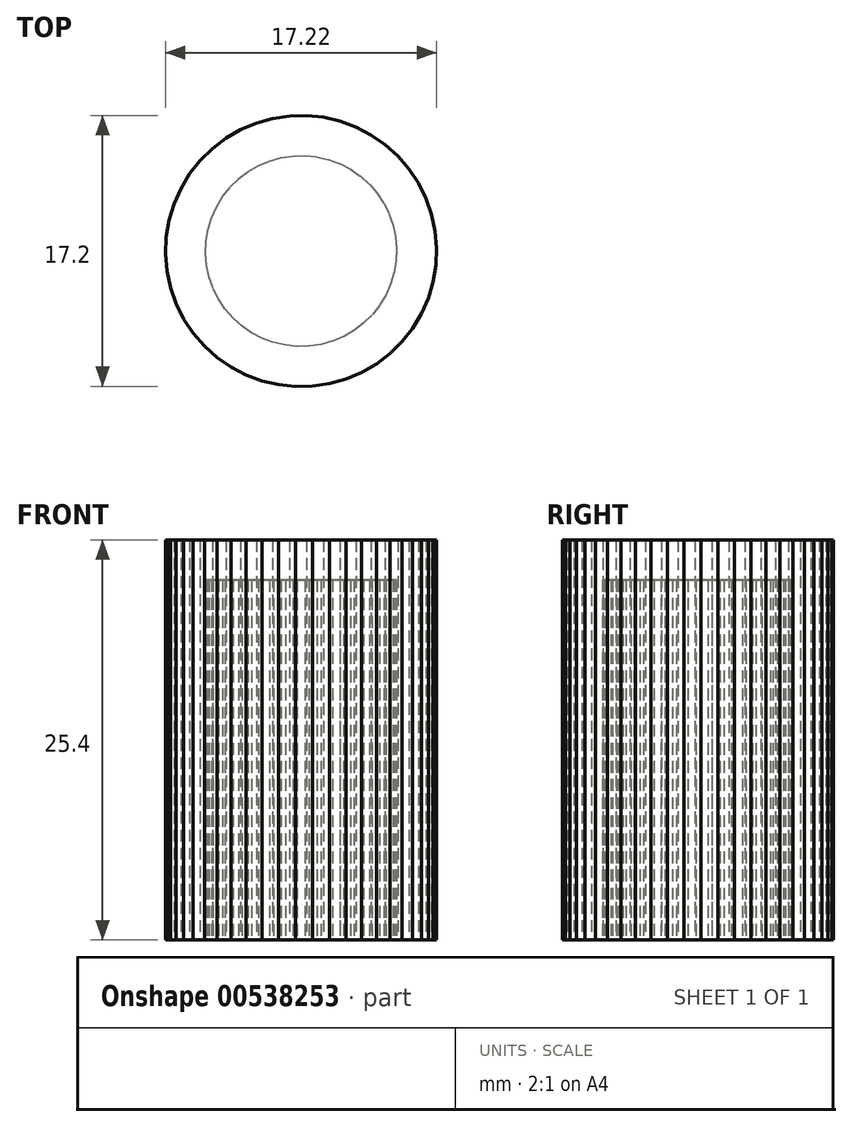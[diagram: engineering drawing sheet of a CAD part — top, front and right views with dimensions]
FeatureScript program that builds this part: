
annotation { "Feature Type Name" : "Feature", "Feature Type Description" : "" }
export const myFeature = defineFeature(function(context is Context, id is Id, definition is map)
    precondition{}
    {
        {
            var Q0;
            Q0=qCreatedBy(makeId("Top.planeOp"),FACE);
            var sketch = newSketch(context, id + "F0", { "sketchPlane" : qUnion([Q0])});
            skCircle(sketch, "E0.cCircle", {"center": v(0, 0) * mm, "radius": 8.61 * mm, "construction": true});
            skLineSegment(sketch, "E0.0", {"start": v(-6.85, -5.21) * mm, "end": v(-7.45, -4.31) * mm});
            skLineSegment(sketch, "E0.1", {"start": v(-7.45, -4.31) * mm, "end": v(-7.94, -3.35) * mm});
            skLineSegment(sketch, "E0.2", {"start": v(-7.94, -3.35) * mm, "end": v(-8.3, -2.33) * mm});
            skLineSegment(sketch, "E0.3", {"start": v(-8.3, -2.33) * mm, "end": v(-8.52, -1.27) * mm});
            skLineSegment(sketch, "E0.4", {"start": v(-8.52, -1.27) * mm, "end": v(-8.6, -0.2) * mm});
            skLineSegment(sketch, "E0.5", {"start": v(-8.6, -0.2) * mm, "end": v(-8.57, 0.9) * mm});
            skLineSegment(sketch, "E0.6", {"start": v(-8.57, 0.9) * mm, "end": v(-8.39, 1.96) * mm});
            skLineSegment(sketch, "E0.7", {"start": v(-8.39, 1.96) * mm, "end": v(-8.08, 3) * mm});
            skLineSegment(sketch, "E0.8", {"start": v(-8.08, 3) * mm, "end": v(-7.64, 3.98) * mm});
            skLineSegment(sketch, "E0.9", {"start": v(-7.64, 3.98) * mm, "end": v(-7.08, 4.9) * mm});
            skLineSegment(sketch, "E0.10", {"start": v(-7.08, 4.9) * mm, "end": v(-6.4, 5.76) * mm});
            skLineSegment(sketch, "E0.11", {"start": v(-6.4, 5.76) * mm, "end": v(-5.63, 6.51) * mm});
            skLineSegment(sketch, "E0.12", {"start": v(-5.63, 6.51) * mm, "end": v(-4.77, 7.17) * mm});
            skLineSegment(sketch, "E0.13", {"start": v(-4.77, 7.17) * mm, "end": v(-3.84, 7.7) * mm});
            skLineSegment(sketch, "E0.14", {"start": v(-3.84, 7.7) * mm, "end": v(-2.84, 8.13) * mm});
            skLineSegment(sketch, "E0.15", {"start": v(-2.84, 8.13) * mm, "end": v(-1.8, 8.42) * mm});
            skLineSegment(sketch, "E0.16", {"start": v(-1.8, 8.42) * mm, "end": v(-0.73, 8.58) * mm});
            skLineSegment(sketch, "E0.17", {"start": v(-0.73, 8.58) * mm, "end": v(0.35, 8.6) * mm});
            skLineSegment(sketch, "E0.18", {"start": v(0.35, 8.6) * mm, "end": v(1.43, 8.5) * mm});
            skLineSegment(sketch, "E0.19", {"start": v(1.43, 8.5) * mm, "end": v(2.48, 8.25) * mm});
            skLineSegment(sketch, "E0.20", {"start": v(2.48, 8.25) * mm, "end": v(3.5, 7.87) * mm});
            skLineSegment(sketch, "E0.21", {"start": v(3.5, 7.87) * mm, "end": v(4.45, 7.37) * mm});
            skLineSegment(sketch, "E0.22", {"start": v(4.45, 7.37) * mm, "end": v(5.34, 6.76) * mm});
            skLineSegment(sketch, "E0.23", {"start": v(5.34, 6.76) * mm, "end": v(6.15, 6.03) * mm});
            skLineSegment(sketch, "E0.24", {"start": v(6.15, 6.03) * mm, "end": v(6.85, 5.21) * mm});
            skLineSegment(sketch, "E0.25", {"start": v(6.85, 5.21) * mm, "end": v(7.45, 4.31) * mm});
            skLineSegment(sketch, "E0.26", {"start": v(7.45, 4.31) * mm, "end": v(7.94, 3.35) * mm});
            skLineSegment(sketch, "E0.27", {"start": v(7.94, 3.35) * mm, "end": v(8.3, 2.33) * mm});
            skLineSegment(sketch, "E0.28", {"start": v(8.3, 2.33) * mm, "end": v(8.52, 1.27) * mm});
            skLineSegment(sketch, "E0.29", {"start": v(8.52, 1.27) * mm, "end": v(8.6, 0.2) * mm});
            skLineSegment(sketch, "E0.30", {"start": v(8.6, 0.2) * mm, "end": v(8.57, -0.9) * mm});
            skLineSegment(sketch, "E0.31", {"start": v(8.57, -0.9) * mm, "end": v(8.39, -1.96) * mm});
            skLineSegment(sketch, "E0.32", {"start": v(8.39, -1.96) * mm, "end": v(8.08, -3) * mm});
            skLineSegment(sketch, "E0.33", {"start": v(8.08, -3) * mm, "end": v(7.64, -3.98) * mm});
            skLineSegment(sketch, "E0.34", {"start": v(7.64, -3.98) * mm, "end": v(7.08, -4.9) * mm});
            skLineSegment(sketch, "E0.35", {"start": v(7.08, -4.9) * mm, "end": v(6.4, -5.76) * mm});
            skLineSegment(sketch, "E0.36", {"start": v(6.4, -5.76) * mm, "end": v(5.63, -6.51) * mm});
            skLineSegment(sketch, "E0.37", {"start": v(5.63, -6.51) * mm, "end": v(4.77, -7.17) * mm});
            skLineSegment(sketch, "E0.38", {"start": v(4.77, -7.17) * mm, "end": v(3.84, -7.7) * mm});
            skLineSegment(sketch, "E0.39", {"start": v(3.84, -7.7) * mm, "end": v(2.84, -8.13) * mm});
            skLineSegment(sketch, "E0.40", {"start": v(2.84, -8.13) * mm, "end": v(1.8, -8.42) * mm});
            skLineSegment(sketch, "E0.41", {"start": v(1.8, -8.42) * mm, "end": v(0.73, -8.58) * mm});
            skLineSegment(sketch, "E0.42", {"start": v(0.73, -8.58) * mm, "end": v(-0.35, -8.6) * mm});
            skLineSegment(sketch, "E0.43", {"start": v(-0.35, -8.6) * mm, "end": v(-1.43, -8.5) * mm});
            skLineSegment(sketch, "E0.44", {"start": v(-1.43, -8.5) * mm, "end": v(-2.48, -8.25) * mm});
            skLineSegment(sketch, "E0.45", {"start": v(-2.48, -8.25) * mm, "end": v(-3.5, -7.87) * mm});
            skLineSegment(sketch, "E0.46", {"start": v(-3.5, -7.87) * mm, "end": v(-4.45, -7.37) * mm});
            skLineSegment(sketch, "E0.47", {"start": v(-4.45, -7.37) * mm, "end": v(-5.34, -6.76) * mm});
            skLineSegment(sketch, "E0.48", {"start": v(-5.34, -6.76) * mm, "end": v(-6.15, -6.03) * mm});
            skLineSegment(sketch, "E0.49", {"start": v(-6.15, -6.03) * mm, "end": v(-6.85, -5.21) * mm});
            skSolve(sketch);
        }
        {
            var Q0;
            Q0 = qSketchRegion(id + "F0", true);
            extrude(context, id + "F1", {"entities" : qUnion([Q0]), "depth" : 25.4 * mm, "offsetDistance" : 25.4 * mm});
        }
        {
            var Q0;
            Q0=makeQuery(id+"F1.opExtrude","CAP_FACE",FACE,{"disambiguationData":[OSD([sQuery(id+"F0.wireOp",EDGE,"E0.0"),sQuery(id+"F0.wireOp",EDGE,"E0.1"),sQuery(id+"F0.wireOp",EDGE,"E0.2"),sQuery(id+"F0.wireOp",EDGE,"E0.3"),sQuery(id+"F0.wireOp",EDGE,"E0.4"),sQuery(id+"F0.wireOp",EDGE,"E0.5"),sQuery(id+"F0.wireOp",EDGE,"E0.6"),sQuery(id+"F0.wireOp",EDGE,"E0.7"),sQuery(id+"F0.wireOp",EDGE,"E0.8"),sQuery(id+"F0.wireOp",EDGE,"E0.9"),sQuery(id+"F0.wireOp",EDGE,"E0.10"),sQuery(id+"F0.wireOp",EDGE,"E0.11"),sQuery(id+"F0.wireOp",EDGE,"E0.12"),sQuery(id+"F0.wireOp",EDGE,"E0.13"),sQuery(id+"F0.wireOp",EDGE,"E0.14"),sQuery(id+"F0.wireOp",EDGE,"E0.15"),sQuery(id+"F0.wireOp",EDGE,"E0.16"),sQuery(id+"F0.wireOp",EDGE,"E0.17"),sQuery(id+"F0.wireOp",EDGE,"E0.18"),sQuery(id+"F0.wireOp",EDGE,"E0.19"),sQuery(id+"F0.wireOp",EDGE,"E0.20"),sQuery(id+"F0.wireOp",EDGE,"E0.21"),sQuery(id+"F0.wireOp",EDGE,"E0.22"),sQuery(id+"F0.wireOp",EDGE,"E0.23"),sQuery(id+"F0.wireOp",EDGE,"E0.24"),sQuery(id+"F0.wireOp",EDGE,"E0.25"),sQuery(id+"F0.wireOp",EDGE,"E0.26"),sQuery(id+"F0.wireOp",EDGE,"E0.27"),sQuery(id+"F0.wireOp",EDGE,"E0.28"),sQuery(id+"F0.wireOp",EDGE,"E0.29"),sQuery(id+"F0.wireOp",EDGE,"E0.30"),sQuery(id+"F0.wireOp",EDGE,"E0.31"),sQuery(id+"F0.wireOp",EDGE,"E0.32"),sQuery(id+"F0.wireOp",EDGE,"E0.33"),sQuery(id+"F0.wireOp",EDGE,"E0.34"),sQuery(id+"F0.wireOp",EDGE,"E0.35"),sQuery(id+"F0.wireOp",EDGE,"E0.36"),sQuery(id+"F0.wireOp",EDGE,"E0.37"),sQuery(id+"F0.wireOp",EDGE,"E0.38"),sQuery(id+"F0.wireOp",EDGE,"E0.39"),sQuery(id+"F0.wireOp",EDGE,"E0.40"),sQuery(id+"F0.wireOp",EDGE,"E0.41"),sQuery(id+"F0.wireOp",EDGE,"E0.42"),sQuery(id+"F0.wireOp",EDGE,"E0.43"),sQuery(id+"F0.wireOp",EDGE,"E0.44"),sQuery(id+"F0.wireOp",EDGE,"E0.45"),sQuery(id+"F0.wireOp",EDGE,"E0.46"),sQuery(id+"F0.wireOp",EDGE,"E0.47"),sQuery(id+"F0.wireOp",EDGE,"E0.48"),sQuery(id+"F0.wireOp",EDGE,"E0.49")])],"isStart":true});
            shell(context, id + "F2", {"entities" : qUnion([Q0]), "thickness" : 2.54 * mm});
        }
        {
            var Q0;
            Q0=makeQuery(id+"F1.opExtrude","SWEPT_BODY",BODY,{"disambiguationData":[OSD([sQuery(id+"F0.wireOp",EDGE,"E0.0"),sQuery(id+"F0.wireOp",EDGE,"E0.1"),sQuery(id+"F0.wireOp",EDGE,"E0.2"),sQuery(id+"F0.wireOp",EDGE,"E0.3"),sQuery(id+"F0.wireOp",EDGE,"E0.4"),sQuery(id+"F0.wireOp",EDGE,"E0.5"),sQuery(id+"F0.wireOp",EDGE,"E0.6"),sQuery(id+"F0.wireOp",EDGE,"E0.7"),sQuery(id+"F0.wireOp",EDGE,"E0.8"),sQuery(id+"F0.wireOp",EDGE,"E0.9"),sQuery(id+"F0.wireOp",EDGE,"E0.10"),sQuery(id+"F0.wireOp",EDGE,"E0.11"),sQuery(id+"F0.wireOp",EDGE,"E0.12"),sQuery(id+"F0.wireOp",EDGE,"E0.13"),sQuery(id+"F0.wireOp",EDGE,"E0.14"),sQuery(id+"F0.wireOp",EDGE,"E0.15"),sQuery(id+"F0.wireOp",EDGE,"E0.16"),sQuery(id+"F0.wireOp",EDGE,"E0.17"),sQuery(id+"F0.wireOp",EDGE,"E0.18"),sQuery(id+"F0.wireOp",EDGE,"E0.19"),sQuery(id+"F0.wireOp",EDGE,"E0.20"),sQuery(id+"F0.wireOp",EDGE,"E0.21"),sQuery(id+"F0.wireOp",EDGE,"E0.22"),sQuery(id+"F0.wireOp",EDGE,"E0.23"),sQuery(id+"F0.wireOp",EDGE,"E0.24"),sQuery(id+"F0.wireOp",EDGE,"E0.25"),sQuery(id+"F0.wireOp",EDGE,"E0.26"),sQuery(id+"F0.wireOp",EDGE,"E0.27"),sQuery(id+"F0.wireOp",EDGE,"E0.28"),sQuery(id+"F0.wireOp",EDGE,"E0.29"),sQuery(id+"F0.wireOp",EDGE,"E0.30"),sQuery(id+"F0.wireOp",EDGE,"E0.31"),sQuery(id+"F0.wireOp",EDGE,"E0.32"),sQuery(id+"F0.wireOp",EDGE,"E0.33"),sQuery(id+"F0.wireOp",EDGE,"E0.34"),sQuery(id+"F0.wireOp",EDGE,"E0.35"),sQuery(id+"F0.wireOp",EDGE,"E0.36"),sQuery(id+"F0.wireOp",EDGE,"E0.37"),sQuery(id+"F0.wireOp",EDGE,"E0.38"),sQuery(id+"F0.wireOp",EDGE,"E0.39"),sQuery(id+"F0.wireOp",EDGE,"E0.40"),sQuery(id+"F0.wireOp",EDGE,"E0.41"),sQuery(id+"F0.wireOp",EDGE,"E0.42"),sQuery(id+"F0.wireOp",EDGE,"E0.43"),sQuery(id+"F0.wireOp",EDGE,"E0.44"),sQuery(id+"F0.wireOp",EDGE,"E0.45"),sQuery(id+"F0.wireOp",EDGE,"E0.46"),sQuery(id+"F0.wireOp",EDGE,"E0.47"),sQuery(id+"F0.wireOp",EDGE,"E0.48"),sQuery(id+"F0.wireOp",EDGE,"E0.49")])]});
            var Q1;
            Q1=makeQuery(id+"F1.opExtrude","SWEPT_EDGE",EDGE,{"disambiguationData":[OSD([sQuery(id+"F0.wireOp",EDGE,"E0.37"),sQuery(id+"F0.wireOp",EDGE,"E0.38")])]});
            transform(context, id + "F3", {"entities" : qUnion([Q0]), "transformType" : TransformType.TRANSLATION_ENTITY, "oppositeDirectionEntity" : false, "transformLine" : qUnion([Q1]), "makeCopy" : false});
        }
    });
